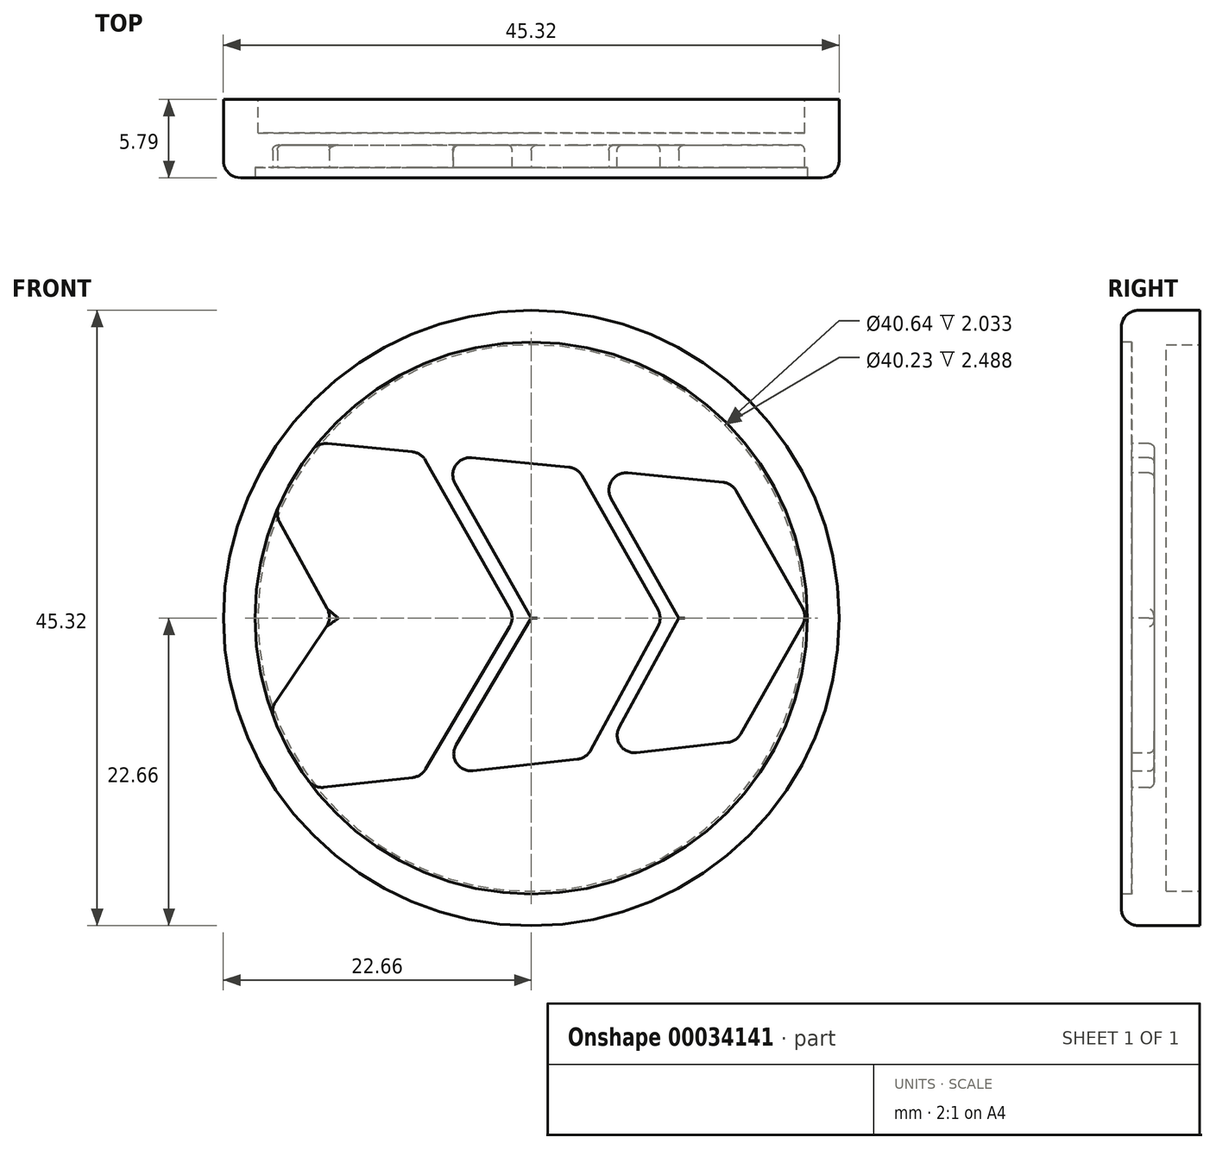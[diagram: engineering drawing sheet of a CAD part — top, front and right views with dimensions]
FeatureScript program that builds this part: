
annotation { "Feature Type Name" : "Feature", "Feature Type Description" : "" }
export const myFeature = defineFeature(function(context is Context, id is Id, definition is map)
    precondition{}
    {
        {
            var Q0;
            Q0=qCreatedBy(makeId("Front.planeOp"),FACE);
            var sketch = newSketch(context, id + "F0", { "sketchPlane" : qUnion([Q0])});
            skCircle(sketch, "E0", {"center": v(0, 0) * mm, "radius": 22.66 * mm});
            skSolve(sketch);
        }
        {
            var Q0;
            Q0 = qSketchRegion(id + "F0", true);
            extrude(context, id + "F1", {"entities" : qUnion([Q0]), "depth" : 5.8 * mm});
        }
        {
            var Q0;
            Q0=makeQuery(id+"F1.opExtrude","CAP_FACE",FACE,{"disambiguationData":[OSD([sQuery(id+"F0.wireOp",EDGE,"E0")])],"isStart":false});
            var sketch = newSketch(context, id + "F2", { "sketchPlane" : qUnion([Q0])});
            skCircle(sketch, "E1", {"center": v(0, 0) * mm, "radius": 20.32 * mm});
            skSolve(sketch);
        }
        {
            var Q0;
            Q0=makeQuery(id+"F2.imprint","IMPRINT",FACE,{"disambiguationData":[TD([[makeQuery(id+"F2.imprint","IMPRINT",EDGE,{"derivedFrom":sQuery(id+"F2.wireOp",EDGE,"E1")}),1.0]])]});
            extrude(context, id + "F3", {"entities" : qUnion([Q0]), "operationType" : NewBodyOperationType.REMOVE, "oppositeDirection" : true, "depth" : 0.76 * mm});
        }
        {
            var Q0;
            Q0=makeQuery(id+"F1.opExtrude","CAP_EDGE",EDGE,{"disambiguationData":[OSD([sQuery(id+"F0.wireOp",EDGE,"E0")])],"isStart":false});
            fillet(context, id + "F4", {"entities" : qUnion([Q0]), "radius" : 1.27 * mm, "tangentPropagation" : true, "allowEdgeOverflow" : false});
        }
        {
            var Q0;
            Q0=makeQuery(id+"F1.opExtrude","CAP_FACE",FACE,{"disambiguationData":[OSD([sQuery(id+"F0.wireOp",EDGE,"E0")])],"isStart":true});
            shell(context, id + "F5", {"entities" : qUnion([Q0]), "thickness" : 2.54 * mm});
        }
        {
            var Q0;
            Q0=makeQuery(id+"F3.boolean.opBoolean","COPY",FACE,{"derivedFrom":makeQuery(id+"F3.opExtrude","CAP_FACE",FACE,{"disambiguationData":[OSD([sQuery(id+"F2.wireOp",EDGE,"E1")])],"isStart":false})});
            var sketch = newSketch(context, id + "F6", { "sketchPlane" : qUnion([Q0])});
            skLineSegment(sketch, "E2", {"start": v(-15.7, 12.9) * mm, "end": v(-8.1, 12.17) * mm});
            skLineSegment(sketch, "E3", {"start": v(-15.98, -12.55) * mm, "end": v(-8.1, -11.67) * mm});
            skLineSegment(sketch, "E4", {"start": v(-6.81, 12.04) * mm, "end": v(0, 0) * mm});
            skLineSegment(sketch, "E5", {"start": v(0, 0) * mm, "end": v(-6.82, -11.53) * mm});
            skLineSegment(sketch, "E6", {"start": v(3.42, 11.04) * mm, "end": v(9.66, 0) * mm});
            skLineSegment(sketch, "E7", {"start": v(9.66, 0) * mm, "end": v(4.06, -10.32) * mm});
            skLineSegment(sketch, "E8", {"start": v(14.77, 9.93) * mm, "end": v(20.32, 0.11) * mm});
            skLineSegment(sketch, "E9", {"start": v(20.32, 0.11) * mm, "end": v(15.1, -9.1) * mm});
            skLineSegment(sketch, "E10", {"start": v(-18.83, 7.64) * mm, "end": v(-14.64, 0) * mm});
            skLineSegment(sketch, "E11", {"start": v(-14.64, 0) * mm, "end": v(-19.18, -6.71) * mm});
            skLineSegment(sketch, "E12", {"start": v(-8.1, 12.17) * mm, "end": v(-1.21, 0) * mm});
            skLineSegment(sketch, "E13", {"start": v(-1.21, 0) * mm, "end": v(-8.1, -11.67) * mm});
            skLineSegment(sketch, "E14", {"start": v(4.67, 10.92) * mm, "end": v(10.85, 0) * mm});
            skLineSegment(sketch, "E15", {"start": v(10.85, 0) * mm, "end": v(5.32, -10.18) * mm});
            skLineSegment(sketch, "E16.trimOffspring", {"start": v(-6.81, 12.04) * mm, "end": v(3.42, 11.04) * mm});
            skLineSegment(sketch, "E17.trimOffspring", {"start": v(4.67, 10.92) * mm, "end": v(14.77, 9.93) * mm});
            skLineSegment(sketch, "E18.trimOffspring", {"start": v(-6.82, -11.53) * mm, "end": v(4.06, -10.32) * mm});
            skLineSegment(sketch, "E19.trimOffspring", {"start": v(5.32, -10.18) * mm, "end": v(15.1, -9.1) * mm});
            skSolve(sketch);
        }
        {
            var Q0;
            Q0 = qSketchRegion(id + "F6", true);
            var Q1;
            {var subQ4=sQuery(id+"F6.wireOp",EDGE,"E2");Q1=makeQuery(id+"F6.imprint","IMPRINT",FACE,{"disambiguationData":[TD([[makeQuery(id+"F6.imprint","IMPRINT",EDGE,{"derivedFrom":subQ4}),-1.0]])]});}
            extrude(context, id + "F7", {"entities" : qUnion([Q0, Q1]), "operationType" : NewBodyOperationType.REMOVE, "oppositeDirection" : true, "depth" : 1.65 * mm});
        }
        {
            var Q0;
            Q0=makeQuery(id+"F7.boolean.opBoolean","COPY",EDGE,{"derivedFrom":makeQuery(id+"F7.opExtrude","CAP_EDGE",EDGE,{"disambiguationData":[OSD([sQuery(id+"F6.wireOp",EDGE,"E14")])],"isStart":false})});
            var Q1;
            Q1=makeQuery(id+"F7.boolean.opBoolean","COPY",EDGE,{"derivedFrom":makeQuery(id+"F7.opExtrude","CAP_EDGE",EDGE,{"disambiguationData":[OSD([sQuery(id+"F6.wireOp",EDGE,"E17.trimOffspring")])],"isStart":false})});
            var Q2;
            Q2=makeQuery(id+"F7.boolean.opBoolean","COPY",EDGE,{"derivedFrom":makeQuery(id+"F7.opExtrude","CAP_EDGE",EDGE,{"disambiguationData":[OSD([sQuery(id+"F6.wireOp",EDGE,"E8")])],"isStart":false})});
            var Q3;
            Q3=makeQuery(id+"F7.boolean.opBoolean","COPY",EDGE,{"derivedFrom":makeQuery(id+"F7.opExtrude","CAP_EDGE",EDGE,{"disambiguationData":[OSD([sQuery(id+"F6.wireOp",EDGE,"E9")])],"isStart":false})});
            var Q4;
            Q4=makeQuery(id+"F7.boolean.opBoolean","COPY",EDGE,{"derivedFrom":makeQuery(id+"F7.opExtrude","CAP_EDGE",EDGE,{"disambiguationData":[OSD([sQuery(id+"F6.wireOp",EDGE,"E19.trimOffspring")])],"isStart":false})});
            var Q5;
            Q5=makeQuery(id+"F7.boolean.opBoolean","COPY",EDGE,{"derivedFrom":makeQuery(id+"F7.opExtrude","CAP_EDGE",EDGE,{"disambiguationData":[OSD([sQuery(id+"F6.wireOp",EDGE,"E15")])],"isStart":false})});
            var Q6;
            Q6=makeQuery(id+"F7.boolean.opBoolean","COPY",EDGE,{"derivedFrom":makeQuery(id+"F7.opExtrude","CAP_EDGE",EDGE,{"disambiguationData":[OSD([sQuery(id+"F6.wireOp",EDGE,"E4")])],"isStart":false})});
            var Q7;
            Q7=makeQuery(id+"F7.boolean.opBoolean","COPY",EDGE,{"derivedFrom":makeQuery(id+"F7.opExtrude","CAP_EDGE",EDGE,{"disambiguationData":[OSD([sQuery(id+"F6.wireOp",EDGE,"E16.trimOffspring")])],"isStart":false})});
            var Q8;
            Q8=makeQuery(id+"F7.boolean.opBoolean","COPY",EDGE,{"derivedFrom":makeQuery(id+"F7.opExtrude","CAP_EDGE",EDGE,{"disambiguationData":[OSD([sQuery(id+"F6.wireOp",EDGE,"E6")])],"isStart":false})});
            var Q9;
            Q9=makeQuery(id+"F7.boolean.opBoolean","COPY",EDGE,{"derivedFrom":makeQuery(id+"F7.opExtrude","CAP_EDGE",EDGE,{"disambiguationData":[OSD([sQuery(id+"F6.wireOp",EDGE,"E5")])],"isStart":false})});
            var Q10;
            Q10=makeQuery(id+"F7.boolean.opBoolean","COPY",EDGE,{"derivedFrom":makeQuery(id+"F7.opExtrude","CAP_EDGE",EDGE,{"disambiguationData":[OSD([sQuery(id+"F6.wireOp",EDGE,"E18.trimOffspring")])],"isStart":false})});
            var Q11;
            Q11=makeQuery(id+"F7.boolean.opBoolean","COPY",EDGE,{"derivedFrom":makeQuery(id+"F7.opExtrude","CAP_EDGE",EDGE,{"disambiguationData":[OSD([sQuery(id+"F6.wireOp",EDGE,"E7")])],"isStart":false})});
            var Q12;
            Q12=makeQuery(id+"F7.boolean.opBoolean","COPY",EDGE,{"derivedFrom":makeQuery(id+"F7.opExtrude","CAP_EDGE",EDGE,{"disambiguationData":[OSD([sQuery(id+"F6.wireOp",EDGE,"E2")])],"isStart":false})});
            var Q13;
            {var subQ0=sQuery(id+"F2.wireOp",EDGE,"E1");var subQ1=makeQuery(id+"F3.boolean.opBoolean","COPY",EDGE,{"derivedFrom":makeQuery(id+"F3.opExtrude","CAP_EDGE",EDGE,{"disambiguationData":[OSD([subQ0])],"isStart":false})});Q13=makeQuery(id+"F7.boolean.opBoolean","COPY",EDGE,{"derivedFrom":makeQuery(id+"F7.opExtrude","CAP_EDGE",EDGE,{"disambiguationData":[OSD([subQ0]),TDD([makeQuery(id+"F6.imprint","IMPRINT",EDGE,{"disambiguationData":[TD([[makeQuery(id+"F6.imprint","INTERSECT",VERTEX,{"derivedFrom":[subQ1,sQuery(id+"F6.wireOp",EDGE,"E2")]}),-1.0]])],"derivedFrom":subQ1})])],"isStart":false})});}
            var Q14;
            Q14=makeQuery(id+"F7.boolean.opBoolean","COPY",EDGE,{"derivedFrom":makeQuery(id+"F7.opExtrude","CAP_EDGE",EDGE,{"disambiguationData":[OSD([sQuery(id+"F6.wireOp",EDGE,"E10")])],"isStart":false})});
            var Q15;
            Q15=makeQuery(id+"F7.boolean.opBoolean","COPY",EDGE,{"derivedFrom":makeQuery(id+"F7.opExtrude","CAP_EDGE",EDGE,{"disambiguationData":[OSD([sQuery(id+"F6.wireOp",EDGE,"E11")])],"isStart":false})});
            var Q16;
            {var subQ0=sQuery(id+"F2.wireOp",EDGE,"E1");var subQ1=makeQuery(id+"F3.boolean.opBoolean","COPY",EDGE,{"derivedFrom":makeQuery(id+"F3.opExtrude","CAP_EDGE",EDGE,{"disambiguationData":[OSD([subQ0])],"isStart":false})});Q16=makeQuery(id+"F7.boolean.opBoolean","COPY",EDGE,{"derivedFrom":makeQuery(id+"F7.opExtrude","CAP_EDGE",EDGE,{"disambiguationData":[OSD([subQ0]),TDD([makeQuery(id+"F6.imprint","IMPRINT",EDGE,{"disambiguationData":[TD([[makeQuery(id+"F6.imprint","INTERSECT",VERTEX,{"derivedFrom":[subQ1,sQuery(id+"F6.wireOp",EDGE,"E3")]}),1.0]])],"derivedFrom":subQ1})])],"isStart":false})});}
            var Q17;
            Q17=makeQuery(id+"F7.boolean.opBoolean","COPY",EDGE,{"derivedFrom":makeQuery(id+"F7.opExtrude","CAP_EDGE",EDGE,{"disambiguationData":[OSD([sQuery(id+"F6.wireOp",EDGE,"E13")])],"isStart":false})});
            var Q18;
            Q18=makeQuery(id+"F7.boolean.opBoolean","COPY",EDGE,{"derivedFrom":makeQuery(id+"F7.opExtrude","CAP_EDGE",EDGE,{"disambiguationData":[OSD([sQuery(id+"F6.wireOp",EDGE,"E12")])],"isStart":false})});
            var Q19;
            Q19=makeQuery(id+"F7.boolean.opBoolean","COPY",EDGE,{"derivedFrom":makeQuery(id+"F7.opExtrude","CAP_EDGE",EDGE,{"disambiguationData":[OSD([sQuery(id+"F6.wireOp",EDGE,"E3")])],"isStart":false})});
            fillet(context, id + "F8", {"entities" : qUnion([Q0, Q1, Q2, Q3, Q4, Q5, Q6, Q7, Q8, Q9, Q10, Q11, Q12, Q13, Q14, Q15, Q16, Q17, Q18, Q19]), "radius" : 0.38 * mm, "tangentPropagation" : true, "allowEdgeOverflow" : false});
        }
        {
            var Q0;
            {var subQ0=sQuery(id+"F6.wireOp",EDGE,"E3");var subQ1=sQuery(id+"F2.wireOp",EDGE,"E1");var subQ2=makeQuery(id+"F3.boolean.opBoolean","COPY",EDGE,{"derivedFrom":makeQuery(id+"F3.opExtrude","CAP_EDGE",EDGE,{"disambiguationData":[OSD([subQ1])],"isStart":false})});Q0=makeQuery(id+"F8.opFillet","BLEND_EDGE",EDGE,{"blendedFrom":[makeQuery(id+"F7.boolean.opBoolean","COPY",EDGE,{"derivedFrom":makeQuery(id+"F7.opExtrude","CAP_EDGE",EDGE,{"disambiguationData":[OSD([subQ0])],"isStart":false})}),makeQuery(id+"F7.boolean.opBoolean","COPY",EDGE,{"derivedFrom":makeQuery(id+"F7.opExtrude","CAP_EDGE",EDGE,{"disambiguationData":[OSD([subQ1]),TDD([makeQuery(id+"F6.imprint","IMPRINT",EDGE,{"disambiguationData":[TD([[makeQuery(id+"F6.imprint","INTERSECT",VERTEX,{"derivedFrom":[subQ2,subQ0]}),1.0]])],"derivedFrom":subQ2})])],"isStart":false})})],"blendedInto":[]});}
            var Q1;
            Q1=makeQuery(id+"F7.boolean.opBoolean","COPY",EDGE,{"derivedFrom":makeQuery(id+"F7.opExtrude","SWEPT_EDGE",EDGE,{"disambiguationData":[OSD([sQuery(id+"F6.wireOp",EDGE,"E10"),sQuery(id+"F6.wireOp",EDGE,"E11")])]})});
            var Q2;
            Q2=makeQuery(id+"F7.boolean.opBoolean","COPY",EDGE,{"derivedFrom":makeQuery(id+"F7.opExtrude","SWEPT_EDGE",EDGE,{"disambiguationData":[OSD([sQuery(id+"F6.wireOp",EDGE,"E5"),sQuery(id+"F6.wireOp",EDGE,"E18.trimOffspring")])]})});
            var Q3;
            Q3=makeQuery(id+"F7.boolean.opBoolean","COPY",EDGE,{"derivedFrom":makeQuery(id+"F7.opExtrude","SWEPT_EDGE",EDGE,{"disambiguationData":[OSD([sQuery(id+"F6.wireOp",EDGE,"E15"),sQuery(id+"F6.wireOp",EDGE,"E19.trimOffspring")])]})});
            var Q4;
            Q4=makeQuery(id+"F7.boolean.opBoolean","COPY",EDGE,{"derivedFrom":makeQuery(id+"F7.opExtrude","SWEPT_EDGE",EDGE,{"disambiguationData":[OSD([sQuery(id+"F2.wireOp",EDGE,"E1"),sQuery(id+"F6.wireOp",EDGE,"E10")])]})});
            var Q5;
            Q5=makeQuery(id+"F7.boolean.opBoolean","COPY",EDGE,{"derivedFrom":makeQuery(id+"F7.opExtrude","SWEPT_EDGE",EDGE,{"disambiguationData":[OSD([sQuery(id+"F2.wireOp",EDGE,"E1"),sQuery(id+"F6.wireOp",EDGE,"E11")])]})});
            var Q6;
            Q6=makeQuery(id+"F7.boolean.opBoolean","COPY",EDGE,{"derivedFrom":makeQuery(id+"F7.opExtrude","SWEPT_EDGE",EDGE,{"disambiguationData":[OSD([sQuery(id+"F6.wireOp",EDGE,"E3"),sQuery(id+"F6.wireOp",EDGE,"E13")])]})});
            var Q7;
            Q7=makeQuery(id+"F7.boolean.opBoolean","COPY",EDGE,{"derivedFrom":makeQuery(id+"F7.opExtrude","SWEPT_EDGE",EDGE,{"disambiguationData":[OSD([sQuery(id+"F6.wireOp",EDGE,"E7"),sQuery(id+"F6.wireOp",EDGE,"E18.trimOffspring")])]})});
            var Q8;
            Q8=makeQuery(id+"F7.boolean.opBoolean","COPY",EDGE,{"derivedFrom":makeQuery(id+"F7.opExtrude","SWEPT_EDGE",EDGE,{"disambiguationData":[OSD([sQuery(id+"F6.wireOp",EDGE,"E9"),sQuery(id+"F6.wireOp",EDGE,"E19.trimOffspring")])]})});
            var Q9;
            Q9=makeQuery(id+"F7.boolean.opBoolean","COPY",EDGE,{"derivedFrom":makeQuery(id+"F7.opExtrude","SWEPT_EDGE",EDGE,{"disambiguationData":[OSD([sQuery(id+"F6.wireOp",EDGE,"E6"),sQuery(id+"F6.wireOp",EDGE,"E7")])]})});
            var Q10;
            Q10=makeQuery(id+"F7.boolean.opBoolean","COPY",EDGE,{"derivedFrom":makeQuery(id+"F7.opExtrude","SWEPT_EDGE",EDGE,{"disambiguationData":[OSD([sQuery(id+"F6.wireOp",EDGE,"E12"),sQuery(id+"F6.wireOp",EDGE,"E13")])]})});
            var Q11;
            Q11=makeQuery(id+"F7.boolean.opBoolean","COPY",EDGE,{"derivedFrom":makeQuery(id+"F7.opExtrude","SWEPT_EDGE",EDGE,{"disambiguationData":[OSD([sQuery(id+"F2.wireOp",EDGE,"E1"),sQuery(id+"F6.wireOp",EDGE,"E8"),sQuery(id+"F6.wireOp",EDGE,"E9")])]})});
            var Q12;
            Q12=makeQuery(id+"F7.boolean.opBoolean","COPY",EDGE,{"derivedFrom":makeQuery(id+"F7.opExtrude","SWEPT_EDGE",EDGE,{"disambiguationData":[OSD([sQuery(id+"F6.wireOp",EDGE,"E8"),sQuery(id+"F6.wireOp",EDGE,"E17.trimOffspring")])]})});
            var Q13;
            Q13=makeQuery(id+"F7.boolean.opBoolean","COPY",EDGE,{"derivedFrom":makeQuery(id+"F7.opExtrude","SWEPT_EDGE",EDGE,{"disambiguationData":[OSD([sQuery(id+"F6.wireOp",EDGE,"E6"),sQuery(id+"F6.wireOp",EDGE,"E16.trimOffspring")])]})});
            var Q14;
            Q14=makeQuery(id+"F7.boolean.opBoolean","COPY",EDGE,{"derivedFrom":makeQuery(id+"F7.opExtrude","SWEPT_EDGE",EDGE,{"disambiguationData":[OSD([sQuery(id+"F6.wireOp",EDGE,"E2"),sQuery(id+"F6.wireOp",EDGE,"E12")])]})});
            var Q15;
            Q15=makeQuery(id+"F7.boolean.opBoolean","COPY",EDGE,{"derivedFrom":makeQuery(id+"F7.opExtrude","SWEPT_EDGE",EDGE,{"disambiguationData":[OSD([sQuery(id+"F2.wireOp",EDGE,"E1"),sQuery(id+"F6.wireOp",EDGE,"E2")])]})});
            var Q16;
            Q16=makeQuery(id+"F8.opFillet","BLEND_EDGE",EDGE,{"blendedFrom":[makeQuery(id+"F7.boolean.opBoolean","COPY",EDGE,{"derivedFrom":makeQuery(id+"F7.opExtrude","CAP_EDGE",EDGE,{"disambiguationData":[OSD([sQuery(id+"F6.wireOp",EDGE,"E4")])],"isStart":false})}),makeQuery(id+"F7.boolean.opBoolean","COPY",EDGE,{"derivedFrom":makeQuery(id+"F7.opExtrude","CAP_EDGE",EDGE,{"disambiguationData":[OSD([sQuery(id+"F6.wireOp",EDGE,"E16.trimOffspring")])],"isStart":false})})],"blendedInto":[]});
            var Q17;
            Q17=makeQuery(id+"F7.boolean.opBoolean","COPY",EDGE,{"derivedFrom":makeQuery(id+"F7.opExtrude","SWEPT_EDGE",EDGE,{"disambiguationData":[OSD([sQuery(id+"F6.wireOp",EDGE,"E14"),sQuery(id+"F6.wireOp",EDGE,"E17.trimOffspring")])]})});
            fillet(context, id + "F9", {"entities" : qUnion([Q0, Q1, Q2, Q3, Q4, Q5, Q6, Q7, Q8, Q9, Q10, Q11, Q12, Q13, Q14, Q15, Q16, Q17]), "radius" : 1.27 * mm, "tangentPropagation" : true, "allowEdgeOverflow" : false});
        }
    });
